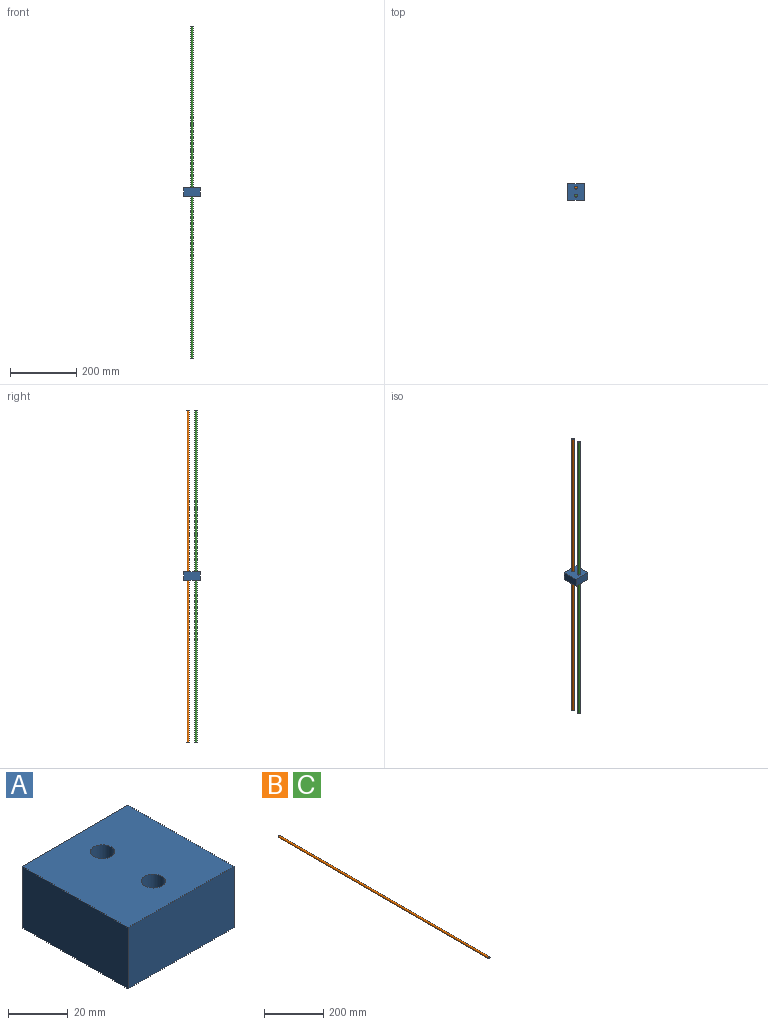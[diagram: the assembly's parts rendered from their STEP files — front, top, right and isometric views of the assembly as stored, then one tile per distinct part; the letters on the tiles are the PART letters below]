
ASSEMBLY  parts=3 mates=2
PART A: 8 faces, bbox 50x50x25 mm
  f0: plane 50x25mm, normal (0,1,0), area 1250mm2, adj f1,f5,f6,f7
  f1: plane 50x25mm, normal (-1,0,0), area 1250mm2, adj f0,f2,f6,f7
  f2: plane 50x25mm, normal (0,-1,0), area 1250mm2, adj f1,f5,f6,f7
  f3: cylinder r=4mm len=25mm, axis (0,0,-1), area 628.3mm2, adj f6,f7
  f4: cylinder r=4mm len=25mm, axis (0,0,-1), area 628.3mm2, adj f6,f7
  f5: plane 50x25mm, normal (1,0,0), area 1250mm2, adj f0,f2,f6,f7
  f6: plane 50x50mm, normal (0,0,1), area 2399.5mm2, adj f0,f1,f2,f3,f4,f5
  f7: plane 50x50mm, normal (0,0,-1), area 2399.5mm2, adj f0,f1,f2,f3,f4,f5
PART B: 3 faces, bbox 8x1000x8 mm
  f0: plane 8x8mm, normal (0,1,0), area 50.3mm2, adj f2
  f1: plane 8x8mm, normal (0,-1,0), area 50.3mm2, adj f2
  f2: cylinder r=4mm len=1000mm, axis (0,-1,0), area 25132.7mm2, adj f0,f1
PART C: same geometry as B
PLACE A at identity
PLACE B rot(axis=(1,0,0),90deg) t=(-31.96,83.46,-490.04)mm
PLACE C rot(axis=(1,0,0),90deg) t=(-31.96,59.46,-490.04)mm
MATE fastened B.f2 <-> A.f4  axis (0,0,-1) through (-147.95,79.46,12.5)mm
MATE fastened C.f2 <-> A.f3  axis (0,0,-1) through (-147.95,55.46,12.5)mm
